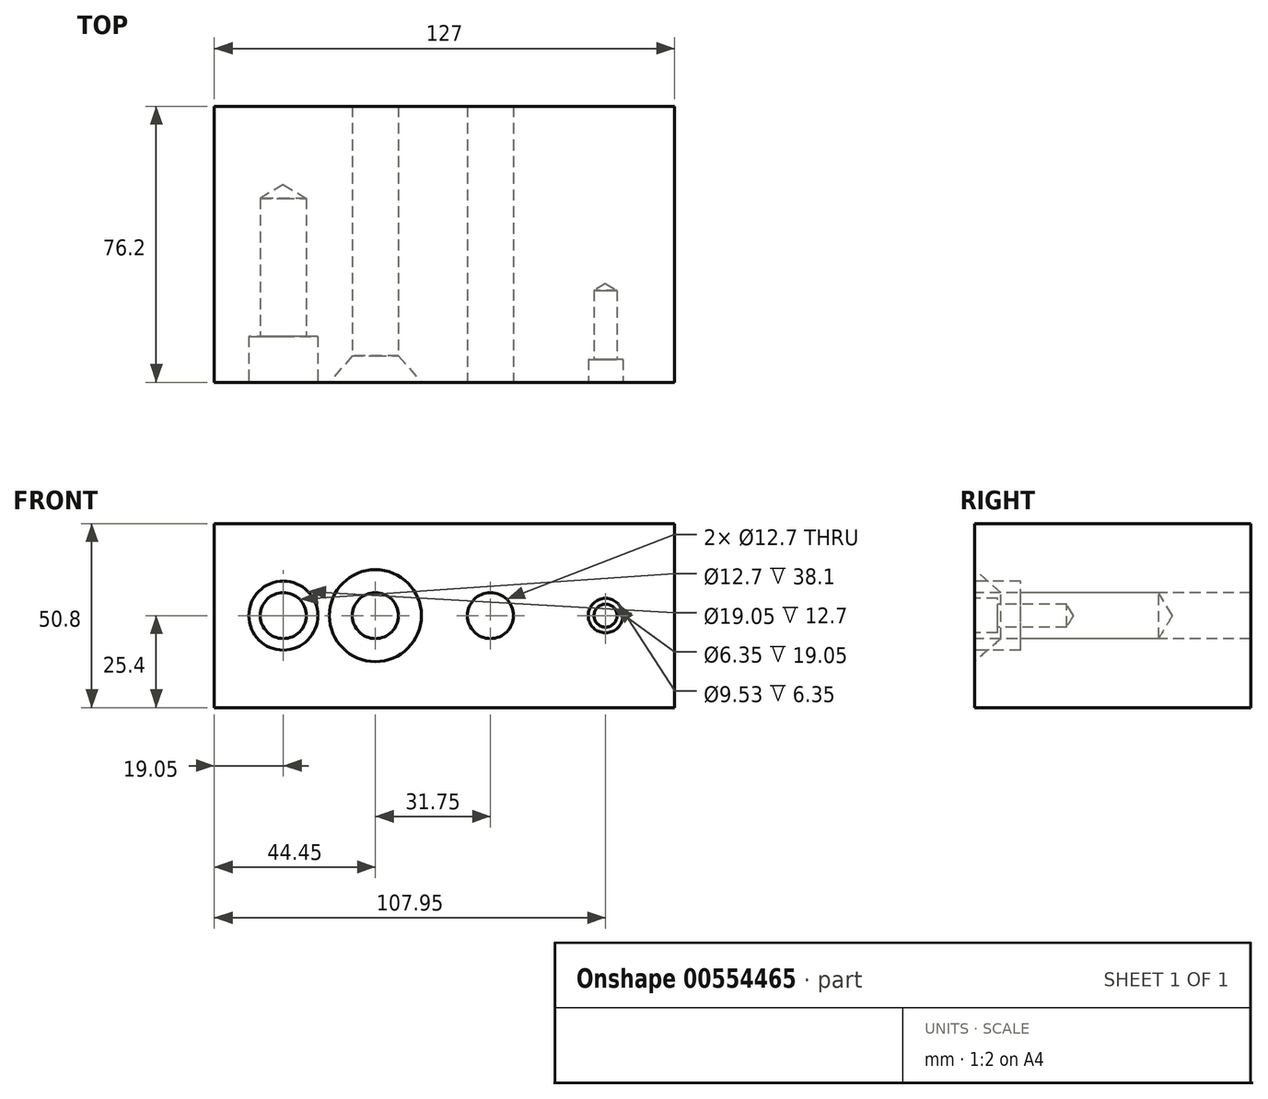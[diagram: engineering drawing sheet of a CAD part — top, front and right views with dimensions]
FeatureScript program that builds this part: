
annotation { "Feature Type Name" : "Feature", "Feature Type Description" : "" }
export const myFeature = defineFeature(function(context is Context, id is Id, definition is map)
    precondition{}
    {
        {
            var Q0;
            Q0=qCreatedBy(makeId("Front.planeOp"),FACE);
            var sketch = newSketch(context, id + "F0", { "sketchPlane" : qUnion([Q0])});
            skLineSegment(sketch, "E0.bottom", {"start": v(0, 0) * mm, "end": v(127, 0) * mm});
            skLineSegment(sketch, "E0.top", {"start": v(0, 50.8) * mm, "end": v(127, 50.8) * mm});
            skLineSegment(sketch, "E0.left", {"start": v(0, 0) * mm, "end": v(0, 50.8) * mm});
            skLineSegment(sketch, "E0.right", {"start": v(127, 0) * mm, "end": v(127, 50.8) * mm});
            skSolve(sketch);
        }
        {
            var Q0;
            Q0=makeQuery(id+"F0.imprint","IMPRINT",FACE,{"disambiguationData":[TD([[makeQuery(id+"F0.imprint","IMPRINT",EDGE,{"derivedFrom":sQuery(id+"F0.wireOp",EDGE,"E0.bottom")}),1.0]])]});
            extrude(context, id + "F1", {"entities" : qUnion([Q0]), "depth" : 76.2 * mm, "offsetDistance" : 25.4 * mm});
        }
        {
            var Q0;
            Q0=makeQuery(id+"F1.opExtrude","CAP_FACE",FACE,{"disambiguationData":[OSD([sQuery(id+"F0.wireOp",EDGE,"E0.bottom"),sQuery(id+"F0.wireOp",EDGE,"E0.top"),sQuery(id+"F0.wireOp",EDGE,"E0.left"),sQuery(id+"F0.wireOp",EDGE,"E0.right")])],"isStart":false});
            var sketch = newSketch(context, id + "F2", { "sketchPlane" : qUnion([Q0])});
            skPoint(sketch, "E1", {"position": v(19.05, 25.4) * mm});
            skPoint(sketch, "E2", {"position": v(44.45, 25.4) * mm});
            skPoint(sketch, "E3", {"position": v(76.2, 25.4) * mm});
            skPoint(sketch, "E4", {"position": v(107.95, 25.4) * mm});
            skSolve(sketch);
        }
        {
            var Q0;
            Q0=sQuery(id+"F2.wireOp",VERTEX,"E1");
            var Q1;
            Q1=makeQuery(id+"F1.opExtrude","SWEPT_BODY",BODY,{"disambiguationData":[OSD([sQuery(id+"F0.wireOp",EDGE,"E0.bottom"),sQuery(id+"F0.wireOp",EDGE,"E0.top"),sQuery(id+"F0.wireOp",EDGE,"E0.left"),sQuery(id+"F0.wireOp",EDGE,"E0.right")])]});
            hole(context, id + "F3", {"style" : HoleStyle.C_BORE, "endStyle" : HoleEndStyle.BLIND, "holeDiameter" : 12.7 * mm, "cBoreDiameter" : 19.05 * mm, "cBoreDepth" : 12.7 * mm, "holeDepth" : 50.8 * mm, "isTappedThrough" : true, "tappedDepth" : 12.7 * mm, "tapClearance" : 3, "locations" : qUnion([Q0]), "scope" : qUnion([Q1])});
        }
        {
            var Q0;
            Q0=sQuery(id+"F2.wireOp",VERTEX,"E2");
            var Q1;
            Q1=makeQuery(id+"F1.opExtrude","SWEPT_BODY",BODY,{"disambiguationData":[OSD([sQuery(id+"F0.wireOp",EDGE,"E0.bottom"),sQuery(id+"F0.wireOp",EDGE,"E0.top"),sQuery(id+"F0.wireOp",EDGE,"E0.left"),sQuery(id+"F0.wireOp",EDGE,"E0.right")])]});
            hole(context, id + "F4", {"style" : HoleStyle.C_SINK, "endStyle" : HoleEndStyle.THROUGH, "holeDiameter" : 12.7 * mm, "cSinkDiameter" : 25.4 * mm, "cSinkAngle" : 82 * degree, "isTappedThrough" : true, "tappedDepth" : 12.7 * mm, "tapClearance" : 3, "locations" : qUnion([Q0]), "scope" : qUnion([Q1])});
        }
        {
            var Q0;
            Q0=sQuery(id+"F2.wireOp",VERTEX,"E3");
            var Q1;
            Q1=makeQuery(id+"F1.opExtrude","SWEPT_BODY",BODY,{"disambiguationData":[OSD([sQuery(id+"F0.wireOp",EDGE,"E0.bottom"),sQuery(id+"F0.wireOp",EDGE,"E0.top"),sQuery(id+"F0.wireOp",EDGE,"E0.left"),sQuery(id+"F0.wireOp",EDGE,"E0.right")])]});
            hole(context, id + "F5", {"style" : HoleStyle.SIMPLE, "endStyle" : HoleEndStyle.THROUGH, "holeDiameter" : 12.7 * mm, "isTappedThrough" : true, "tappedDepth" : 12.7 * mm, "tapClearance" : 3, "locations" : qUnion([Q0]), "scope" : qUnion([Q1])});
        }
        {
            var Q0;
            Q0=sQuery(id+"F2.wireOp",VERTEX,"E4");
            var Q1;
            Q1=makeQuery(id+"F1.opExtrude","SWEPT_BODY",BODY,{"disambiguationData":[OSD([sQuery(id+"F0.wireOp",EDGE,"E0.bottom"),sQuery(id+"F0.wireOp",EDGE,"E0.top"),sQuery(id+"F0.wireOp",EDGE,"E0.left"),sQuery(id+"F0.wireOp",EDGE,"E0.right")])]});
            hole(context, id + "F6", {"style" : HoleStyle.C_BORE, "endStyle" : HoleEndStyle.BLIND, "holeDiameter" : 6.35 * mm, "cBoreDiameter" : 9.52 * mm, "cBoreDepth" : 6.35 * mm, "holeDepth" : 25.4 * mm, "isTappedThrough" : true, "tappedDepth" : 12.7 * mm, "tapClearance" : 3, "locations" : qUnion([Q0]), "scope" : qUnion([Q1])});
        }
    });
